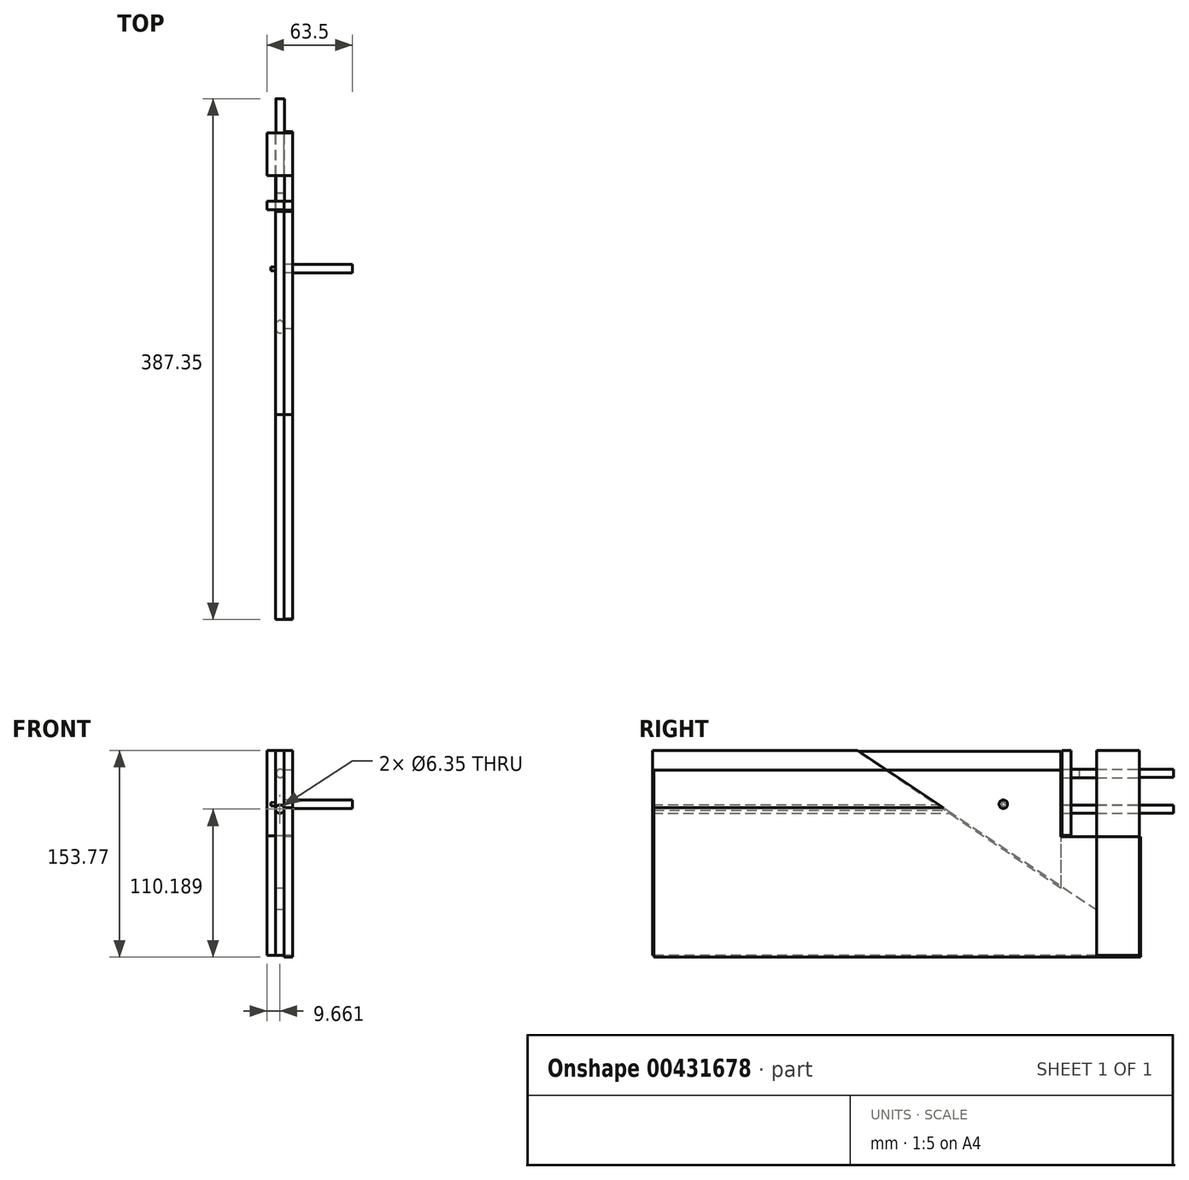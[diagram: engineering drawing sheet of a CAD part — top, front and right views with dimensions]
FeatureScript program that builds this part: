
annotation { "Feature Type Name" : "Feature", "Feature Type Description" : "" }
export const myFeature = defineFeature(function(context is Context, id is Id, definition is map)
    precondition{}
    {
        {
            var Q0;
            Q0=qCreatedBy(makeId("Right.planeOp"),FACE);
            var sketch = newSketch(context, id + "F0", { "sketchPlane" : qUnion([Q0])});
            skLineSegment(sketch, "E0.bottom", {"start": v(165.1, -76.2) * mm, "end": v(-165.1, -76.2) * mm});
            skLineSegment(sketch, "E0.left", {"start": v(165.1, -76.2) * mm, "end": v(165.1, 76.2) * mm});
            skLineSegment(sketch, "E0.right", {"start": v(-165.1, -76.2) * mm, "end": v(-165.1, 76.2) * mm});
            skPoint(sketch, "E0.middle", {"position": v(0, 0) * mm});
            skLineSegment(sketch, "E1.bottom", {"start": v(165.1, 76.2) * mm, "end": v(190.5, 76.2) * mm});
            skLineSegment(sketch, "E1.top", {"start": v(165.1, -76.2) * mm, "end": v(190.5, -76.2) * mm});
            skLineSegment(sketch, "E1.left", {"start": v(165.1, 76.2) * mm, "end": v(165.1, -76.2) * mm});
            skLineSegment(sketch, "E1.right", {"start": v(190.5, 76.2) * mm, "end": v(190.5, -76.2) * mm});
            skPoint(sketch, "E2.endSnap0", {"position": v(165.1, 0) * mm});
            skPoint(sketch, "E3.end.orphan", {"position": v(0, 76.2) * mm});
            skLineSegment(sketch, "E4", {"start": v(-165.1, 76.2) * mm, "end": v(-12.7, 76.2) * mm});
            skLineSegment(sketch, "E5", {"start": v(190.5, 76.2) * mm, "end": v(165.1, 76.2) * mm});
            skLineSegment(sketch, "E6", {"start": v(139.7, 12.7) * mm, "end": v(139.7, 76.2) * mm});
            skLineSegment(sketch, "E7", {"start": v(146.05, 76.2) * mm, "end": v(146.05, 12.7) * mm});
            skLineSegment(sketch, "E8.trimOffspring", {"start": v(146.05, 76.2) * mm, "end": v(139.7, 76.2) * mm});
            skLineSegment(sketch, "E9", {"start": v(139.7, 12.7) * mm, "end": v(146.05, 12.7) * mm});
            skPoint(sketch, "E10.orphan", {"position": v(146.05, 0) * mm});
            skPoint(sketch, "E2.end.orphan", {"position": v(139.7, 0) * mm});
            skLineSegment(sketch, "E11", {"start": v(165.1, -76.2) * mm, "end": v(165.1, -42.09) * mm});
            skLineSegment(sketch, "E12", {"start": v(-12.7, 76.2) * mm, "end": v(165.1, -42.09) * mm});
            skLineSegment(sketch, "E13", {"start": v(-12.7, 76.2) * mm, "end": v(139.7, 76.2) * mm});
            skLineSegment(sketch, "E14", {"start": v(139.7, 12.7) * mm, "end": v(139.7, -25.2) * mm});
            skSolve(sketch);
        }
        {
            var Q0;
            Q0=makeQuery(id+"F0.imprint","IMPRINT",FACE,{"disambiguationData":[TD([[makeQuery(id+"F0.imprint","IMPRINT",EDGE,{"derivedFrom":sQuery(id+"F0.wireOp",EDGE,"E6")}),-1.0]])]});
            var Q1;
            Q1=makeQuery(id+"F0.imprint","IMPRINT",FACE,{"disambiguationData":[TD([[makeQuery(id+"F0.imprint","IMPRINT",EDGE,{"derivedFrom":sQuery(id+"F0.wireOp",EDGE,"E0.bottom")}),-1.0]])]});
            var Q2;
            Q2=makeQuery(id+"F0.imprint","IMPRINT",FACE,{"disambiguationData":[TD([[makeQuery(id+"F0.imprint","IMPRINT",EDGE,{"derivedFrom":sQuery(id+"F0.wireOp",EDGE,"E1.top")}),1.0]])]});
            extrude(context, id + "F1", {"entities" : qUnion([Q0, Q1, Q2]), "depth" : 6.35 * mm});
        }
        {
            var Q0;
            Q0=makeQuery(id+"F1.opExtrude","CAP_FACE",FACE,{"disambiguationData":[OSD([sQuery(id+"F0.wireOp",EDGE,"E0.bottom"),sQuery(id+"F0.wireOp",EDGE,"E0.right"),sQuery(id+"F0.wireOp",EDGE,"E1.top"),sQuery(id+"F0.wireOp",EDGE,"E1.left"),sQuery(id+"F0.wireOp",EDGE,"E1.right"),sQuery(id+"F0.wireOp",EDGE,"E4"),sQuery(id+"F0.wireOp",EDGE,"E5"),sQuery(id+"F0.wireOp",EDGE,"E12")])],"isStart":false});
            var sketch = newSketch(context, id + "F2", { "sketchPlane" : qUnion([Q0])});
            skLineSegment(sketch, "E15.bottom", {"start": v(165.1, 76.2) * mm, "end": v(190.5, 76.2) * mm});
            skLineSegment(sketch, "E15.top", {"start": v(165.1, -76.2) * mm, "end": v(190.5, -76.2) * mm});
            skLineSegment(sketch, "E15.left", {"start": v(165.1, 76.2) * mm, "end": v(165.1, -76.2) * mm});
            skLineSegment(sketch, "E15.right", {"start": v(190.5, 76.2) * mm, "end": v(190.5, -76.2) * mm});
            skSolve(sketch);
        }
        {
            var Q0;
            Q0 = qSketchRegion(id + "F2", true);
            extrude(context, id + "F3", {"entities" : qUnion([Q0]), "operationType" : NewBodyOperationType.ADD, "depth" : 6.35 * mm});
        }
        {
            var Q0;
            Q0=makeQuery(id+"F1.opExtrude","CAP_FACE",FACE,{"disambiguationData":[OSD([sQuery(id+"F0.wireOp",EDGE,"E0.bottom"),sQuery(id+"F0.wireOp",EDGE,"E0.right"),sQuery(id+"F0.wireOp",EDGE,"E1.top"),sQuery(id+"F0.wireOp",EDGE,"E1.left"),sQuery(id+"F0.wireOp",EDGE,"E1.right"),sQuery(id+"F0.wireOp",EDGE,"E4"),sQuery(id+"F0.wireOp",EDGE,"E5"),sQuery(id+"F0.wireOp",EDGE,"E12")])],"isStart":true});
            var sketch = newSketch(context, id + "F4", { "sketchPlane" : qUnion([Q0])});
            skLineSegment(sketch, "E16.bottom", {"start": v(-190.5, 76.2) * mm, "end": v(-165.1, 76.2) * mm});
            skLineSegment(sketch, "E16.top", {"start": v(-190.5, -76.2) * mm, "end": v(-165.1, -76.2) * mm});
            skLineSegment(sketch, "E16.left", {"start": v(-190.5, 76.2) * mm, "end": v(-190.5, -76.2) * mm});
            skLineSegment(sketch, "E16.right", {"start": v(-165.1, 76.2) * mm, "end": v(-165.1, -76.2) * mm});
            skSolve(sketch);
        }
        {
            var Q0;
            Q0 = qSketchRegion(id + "F4", true);
            extrude(context, id + "F5", {"entities" : qUnion([Q0]), "operationType" : NewBodyOperationType.ADD, "depth" : 6.35 * mm});
        }
        {
            var Q0;
            Q0=makeQuery(id+"F1.opExtrude","CAP_FACE",FACE,{"disambiguationData":[OSD([sQuery(id+"F0.wireOp",EDGE,"E0.bottom"),sQuery(id+"F0.wireOp",EDGE,"E0.right"),sQuery(id+"F0.wireOp",EDGE,"E1.top"),sQuery(id+"F0.wireOp",EDGE,"E1.left"),sQuery(id+"F0.wireOp",EDGE,"E1.right"),sQuery(id+"F0.wireOp",EDGE,"E4"),sQuery(id+"F0.wireOp",EDGE,"E5"),sQuery(id+"F0.wireOp",EDGE,"E12")])],"isStart":false});
            var sketch = newSketch(context, id + "F6", { "sketchPlane" : qUnion([Q0])});
            skLineSegment(sketch, "E17.bottom", {"start": v(139.43, 76.32) * mm, "end": v(146.17, 76.32) * mm});
            skLineSegment(sketch, "E17.top", {"start": v(139.43, 13.2) * mm, "end": v(146.17, 13.2) * mm});
            skLineSegment(sketch, "E17.left", {"start": v(139.43, 76.32) * mm, "end": v(139.43, 13.2) * mm});
            skLineSegment(sketch, "E17.right", {"start": v(146.17, 76.32) * mm, "end": v(146.17, 13.2) * mm});
            skSolve(sketch);
        }
        {
            var Q0;
            Q0 = qSketchRegion(id + "F6", true);
            extrude(context, id + "F7", {"entities" : qUnion([Q0]), "operationType" : NewBodyOperationType.ADD, "depth" : 6.35 * mm});
        }
        {
            var Q0;
            Q0=makeQuery(id+"F1.opExtrude","CAP_FACE",FACE,{"disambiguationData":[OSD([sQuery(id+"F0.wireOp",EDGE,"E6"),sQuery(id+"F0.wireOp",EDGE,"E7"),sQuery(id+"F0.wireOp",EDGE,"E8.trimOffspring"),sQuery(id+"F0.wireOp",EDGE,"E9")])],"isStart":true});
            extrude(context, id + "F8", {"entities" : qUnion([Q0]), "operationType" : NewBodyOperationType.ADD, "depth" : 6.35 * mm});
        }
        {
            var Q0;
            Q0=makeQuery(id+"F5.boolean.opBoolean","MERGE",FACE,{"derivedFrom":[makeQuery(id+"F3.boolean.opBoolean","MERGE",FACE,{"derivedFrom":[makeQuery(id+"F1.opExtrude","SWEPT_FACE",FACE,{"disambiguationData":[OSD([sQuery(id+"F0.wireOp",EDGE,"E1.right")])]}),makeQuery(id+"F3.opExtrude","SWEPT_FACE",FACE,{"disambiguationData":[OSD([sQuery(id+"F2.wireOp",EDGE,"E15.right")])]})]}),makeQuery(id+"F5.opExtrude","SWEPT_FACE",FACE,{"disambiguationData":[OSD([sQuery(id+"F4.wireOp",EDGE,"E16.left")])]})]});
            var sketch = newSketch(context, id + "F9", { "sketchPlane" : qUnion([Q0])});
            skPoint(sketch, "E18", {"position": v(-3.08, 38.07) * mm});
            skSolve(sketch);
        }
        {
            var Q0;
            {var subQ0=sQuery(id+"F2.wireOp",EDGE,"E15.right");Q0=makeQuery(id+"F9.imprint","IMPRINT",FACE,{"disambiguationData":[TD([[makeQuery(id+"F9.imprint","IMPRINT",EDGE,{"derivedFrom":makeQuery(id+"F3.opExtrude","CAP_EDGE",EDGE,{"disambiguationData":[OSD([subQ0])],"isStart":false})}),1.0]])]});}
            extrude(context, id + "F10", {"entities" : qUnion([Q0]), "operationType" : NewBodyOperationType.ADD, "depth" : 6.35 * mm});
        }
        {
            var Q0;
            Q0=makeQuery(id+"F10.opExtrude","CAP_FACE",FACE,{"disambiguationData":[OSD([sQuery(id+"F0.wireOp",EDGE,"E1.top"),sQuery(id+"F0.wireOp",EDGE,"E1.right"),sQuery(id+"F0.wireOp",EDGE,"E5"),sQuery(id+"F2.wireOp",EDGE,"E15.bottom"),sQuery(id+"F2.wireOp",EDGE,"E15.top"),sQuery(id+"F2.wireOp",EDGE,"E15.right"),sQuery(id+"F4.wireOp",EDGE,"E16.bottom"),sQuery(id+"F4.wireOp",EDGE,"E16.top"),sQuery(id+"F4.wireOp",EDGE,"E16.left")])],"isStart":false});
            var sketch = newSketch(context, id + "F11", { "sketchPlane" : qUnion([Q0])});
            skCircle(sketch, "E19", {"center": v(-3.31, 32.74) * mm, "radius": 3.18 * mm});
            skSolve(sketch);
        }
        {
            var Q0;
            Q0=sQuery(id+"F11.wireOp",VERTEX,"E19.center");
            var Q1;
            Q1=makeQuery(id+"F1.opExtrude","SWEPT_BODY",BODY,{"disambiguationData":[OSD([sQuery(id+"F0.wireOp",EDGE,"E0.bottom"),sQuery(id+"F0.wireOp",EDGE,"E0.right"),sQuery(id+"F0.wireOp",EDGE,"E1.top"),sQuery(id+"F0.wireOp",EDGE,"E1.left"),sQuery(id+"F0.wireOp",EDGE,"E1.right"),sQuery(id+"F0.wireOp",EDGE,"E4"),sQuery(id+"F0.wireOp",EDGE,"E5"),sQuery(id+"F0.wireOp",EDGE,"E12")])]});
            var Q2;
            Q2=makeQuery(id+"F1.opExtrude","SWEPT_BODY",BODY,{"disambiguationData":[OSD([sQuery(id+"F0.wireOp",EDGE,"E6"),sQuery(id+"F0.wireOp",EDGE,"E7"),sQuery(id+"F0.wireOp",EDGE,"E8.trimOffspring"),sQuery(id+"F0.wireOp",EDGE,"E9")])]});
            hole(context, id + "F12", {"style" : HoleStyle.SIMPLE, "endStyle" : HoleEndStyle.THROUGH, "holeDiameter" : 6.35 * mm, "isTappedThrough" : true, "tappedDepth" : 12.7 * mm, "tapClearance" : 3, "locations" : qUnion([Q0]), "scope" : qUnion([Q1, Q2])});
        }
        {
            var Q0;
            Q0=makeQuery(id+"F10.opExtrude","CAP_FACE",FACE,{"disambiguationData":[OSD([sQuery(id+"F0.wireOp",EDGE,"E1.top"),sQuery(id+"F0.wireOp",EDGE,"E1.right"),sQuery(id+"F0.wireOp",EDGE,"E5"),sQuery(id+"F2.wireOp",EDGE,"E15.bottom"),sQuery(id+"F2.wireOp",EDGE,"E15.top"),sQuery(id+"F2.wireOp",EDGE,"E15.right"),sQuery(id+"F4.wireOp",EDGE,"E16.bottom"),sQuery(id+"F4.wireOp",EDGE,"E16.top"),sQuery(id+"F4.wireOp",EDGE,"E16.left")])],"isStart":false});
            var sketch = newSketch(context, id + "F13", { "sketchPlane" : qUnion([Q0])});
            skCircle(sketch, "E20", {"center": v(-3.31, 32.74) * mm, "radius": 3 * mm});
            skSolve(sketch);
        }
        {
            var Q0;
            Q0 = qSketchRegion(id + "F13", true);
            extrude(context, id + "F14", {"entities" : qUnion([Q0]), "oppositeDirection" : true, "depth" : 58.5 * mm});
        }
        {
            var Q0;
            Q0=makeQuery(id+"F14.opExtrude","CAP_FACE",FACE,{"disambiguationData":[OSD([sQuery(id+"F13.wireOp",EDGE,"E20")])],"isStart":true});
            extrude(context, id + "F15", {"entities" : qUnion([Q0]), "operationType" : NewBodyOperationType.ADD, "depth" : 25.4 * mm});
        }
        {
            var Q0;
            Q0=makeQuery(id+"F10.opExtrude","CAP_FACE",FACE,{"disambiguationData":[OSD([sQuery(id+"F0.wireOp",EDGE,"E1.top"),sQuery(id+"F0.wireOp",EDGE,"E1.right"),sQuery(id+"F0.wireOp",EDGE,"E5"),sQuery(id+"F2.wireOp",EDGE,"E15.bottom"),sQuery(id+"F2.wireOp",EDGE,"E15.top"),sQuery(id+"F2.wireOp",EDGE,"E15.right"),sQuery(id+"F4.wireOp",EDGE,"E16.bottom"),sQuery(id+"F4.wireOp",EDGE,"E16.top"),sQuery(id+"F4.wireOp",EDGE,"E16.left")])],"isStart":false});
            var sketch = newSketch(context, id + "F16", { "sketchPlane" : qUnion([Q0])});
            skCircle(sketch, "E21", {"center": v(-3.68, 59.03) * mm, "radius": 3.18 * mm});
            skSolve(sketch);
        }
        {
            var Q0;
            Q0=sQuery(id+"F16.wireOp",EDGE,"E21");
            extrude(context, id + "F17", {"bodyType" : ToolBodyType.SURFACE, "surfaceEntities" : qUnion([Q0]), "depth" : 25.4 * mm});
        }
        {
            var Q0;
            Q0=makeQuery(id+"F10.opExtrude","CAP_FACE",FACE,{"disambiguationData":[OSD([sQuery(id+"F0.wireOp",EDGE,"E1.top"),sQuery(id+"F0.wireOp",EDGE,"E1.right"),sQuery(id+"F0.wireOp",EDGE,"E5"),sQuery(id+"F2.wireOp",EDGE,"E15.bottom"),sQuery(id+"F2.wireOp",EDGE,"E15.top"),sQuery(id+"F2.wireOp",EDGE,"E15.right"),sQuery(id+"F4.wireOp",EDGE,"E16.bottom"),sQuery(id+"F4.wireOp",EDGE,"E16.top"),sQuery(id+"F4.wireOp",EDGE,"E16.left")])],"isStart":false});
            var sketch = newSketch(context, id + "F18", { "sketchPlane" : qUnion([Q0])});
            skCircle(sketch, "E22", {"center": v(-3.6, 59.3) * mm, "radius": 3.04 * mm});
            skSolve(sketch);
        }
        {
            var Q0;
            Q0 = qSketchRegion(id + "F18", true);
            extrude(context, id + "F19", {"entities" : qUnion([Q0]), "operationType" : NewBodyOperationType.ADD, "depth" : 25.4 * mm});
        }
        {
            var Q0;
            Q0=makeQuery(id+"F19.opExtrude","CAP_FACE",FACE,{"disambiguationData":[OSD([sQuery(id+"F18.wireOp",EDGE,"E22")])],"isStart":false});
            extrude(context, id + "F20", {"entities" : qUnion([Q0]), "operationType" : NewBodyOperationType.ADD, "oppositeDirection" : true, "depth" : 70.16 * mm});
        }
        {
            var Q0;
            Q0=makeQuery(id+"F10.opExtrude","CAP_FACE",FACE,{"disambiguationData":[OSD([sQuery(id+"F0.wireOp",EDGE,"E1.top"),sQuery(id+"F0.wireOp",EDGE,"E1.right"),sQuery(id+"F0.wireOp",EDGE,"E5"),sQuery(id+"F2.wireOp",EDGE,"E15.bottom"),sQuery(id+"F2.wireOp",EDGE,"E15.top"),sQuery(id+"F2.wireOp",EDGE,"E15.right"),sQuery(id+"F4.wireOp",EDGE,"E16.bottom"),sQuery(id+"F4.wireOp",EDGE,"E16.top"),sQuery(id+"F4.wireOp",EDGE,"E16.left")])],"isStart":false});
            var sketch = newSketch(context, id + "F21", { "sketchPlane" : qUnion([Q0])});
            skCircle(sketch, "E23", {"center": v(-3.6, 59.3) * mm, "radius": 3.15 * mm});
            skSolve(sketch);
        }
        {
            var Q0;
            Q0 = qSketchRegion(id + "F21", true);
            extrude(context, id + "F22", {"entities" : qUnion([Q0]), "oppositeDirection" : true, "depth" : 58.5 * mm});
        }
        {
            var Q0;
            Q0=qCreatedBy(makeId("Right.planeOp"),FACE);
            var sketch = newSketch(context, id + "F23", { "sketchPlane" : qUnion([Q0])});
            skLineSegment(sketch, "E24", {"start": v(-13.06, 75.72) * mm, "end": v(138.54, 75.72) * mm});
            skLineSegment(sketch, "E25", {"start": v(138.54, 75.72) * mm, "end": v(138.54, -26.34) * mm});
            skLineSegment(sketch, "E26", {"start": v(138.54, -26.34) * mm, "end": v(-13.06, 75.72) * mm});
            skSolve(sketch);
        }
        {
            var Q0;
            Q0=makeQuery(id+"F23.imprint","IMPRINT",FACE,{"disambiguationData":[TD([[makeQuery(id+"F23.imprint","IMPRINT",EDGE,{"derivedFrom":sQuery(id+"F23.wireOp",EDGE,"E24")}),-1.0]])]});
            extrude(context, id + "F24", {"entities" : qUnion([Q0]), "depth" : 6.35 * mm});
        }
        {
            var Q0;
            Q0=makeQuery(id+"F24.opExtrude","CAP_FACE",FACE,{"disambiguationData":[OSD([sQuery(id+"F23.wireOp",EDGE,"E24"),sQuery(id+"F23.wireOp",EDGE,"E25"),sQuery(id+"F23.wireOp",EDGE,"E26")])],"isStart":false});
            var sketch = newSketch(context, id + "F25", { "sketchPlane" : qUnion([Q0])});
            skCircle(sketch, "E27", {"center": v(95.75, 36.37) * mm, "radius": 3.18 * mm});
            skSolve(sketch);
        }
        {
            var Q0;
            Q0 = qSketchRegion(id + "F25", true);
            extrude(context, id + "F26", {"entities" : qUnion([Q0]), "operationType" : NewBodyOperationType.ADD, "depth" : 25.4 * mm});
        }
        {
            var Q0;
            Q0=makeQuery(id+"F26.opExtrude","CAP_FACE",FACE,{"disambiguationData":[OSD([sQuery(id+"F25.wireOp",EDGE,"E27")])],"isStart":false});
            extrude(context, id + "F27", {"entities" : qUnion([Q0]), "operationType" : NewBodyOperationType.ADD, "oppositeDirection" : true, "depth" : 35.07 * mm, "hasDraft" : true, "draftAngle" : 3 * degree, "draftPullDirection" : true, "hasSecondDirection" : true, "secondDirectionOppositeDirection" : false, "secondDirectionDepth" : 25.4 * mm});
        }
        {
            var Q0;
            {var subQ0=sQuery(id+"F0.wireOp",EDGE,"E0.right");var subQ1=sQuery(id+"F0.wireOp",EDGE,"E4");var subQ2=sQuery(id+"F0.wireOp",EDGE,"E12");Q0=makeQuery(id+"F12.hole-0.boolean.opBoolean","SPLIT",FACE,{"disambiguationData":[TD([makeQuery(id+"F1.opExtrude","SWEPT_FACE",FACE,{"disambiguationData":[OSD([subQ1])]})])],"derivedFrom":makeQuery(id+"F1.opExtrude","CAP_FACE",FACE,{"disambiguationData":[OSD([sQuery(id+"F0.wireOp",EDGE,"E0.bottom"),subQ0,sQuery(id+"F0.wireOp",EDGE,"E1.top"),sQuery(id+"F0.wireOp",EDGE,"E1.left"),sQuery(id+"F0.wireOp",EDGE,"E1.right"),subQ1,sQuery(id+"F0.wireOp",EDGE,"E5"),subQ2])],"isStart":false})});}
            var sketch = newSketch(context, id + "F28", { "sketchPlane" : qUnion([Q0])});
            skSolve(sketch);
        }
        {
            var Q0;
            Q0=makeQuery(id+"F24.opExtrude","CAP_FACE",FACE,{"disambiguationData":[OSD([sQuery(id+"F23.wireOp",EDGE,"E24"),sQuery(id+"F23.wireOp",EDGE,"E25"),sQuery(id+"F23.wireOp",EDGE,"E26")])],"isStart":false});
            var sketch = newSketch(context, id + "F29", { "sketchPlane" : qUnion([Q0])});
            skLineSegment(sketch, "E28.bottom", {"start": v(138.54, 61.78) * mm, "end": v(-164, 61.78) * mm});
            skLineSegment(sketch, "E28.top", {"start": v(138.54, -77.45) * mm, "end": v(-164, -77.45) * mm});
            skLineSegment(sketch, "E28.left", {"start": v(138.54, 61.78) * mm, "end": v(138.54, -77.45) * mm});
            skLineSegment(sketch, "E28.right", {"start": v(-164, 61.78) * mm, "end": v(-164, -77.45) * mm});
            skLineSegment(sketch, "E29", {"start": v(138.54, -77.45) * mm, "end": v(197.86, -77.45) * mm});
            skLineSegment(sketch, "E30", {"start": v(197.86, -77.45) * mm, "end": v(197.86, 0) * mm});
            skLineSegment(sketch, "E31", {"start": v(138.54, 12.07) * mm, "end": v(199.24, 12.07) * mm});
            skLineSegment(sketch, "E32", {"start": v(197.86, 12.07) * mm, "end": v(197.86, -38.73) * mm});
            skLineSegment(sketch, "E33", {"start": v(197.86, -38.73) * mm, "end": v(197.86, 12.07) * mm});
            skSolve(sketch);
        }
        {
            var Q0;
            Q0=makeQuery(id+"F29.imprint","IMPRINT",FACE,{"disambiguationData":[TD([[makeQuery(id+"F29.imprint","IMPRINT",EDGE,{"derivedFrom":makeQuery(id+"F26.opExtrude","CAP_EDGE",EDGE,{"disambiguationData":[OSD([sQuery(id+"F25.wireOp",EDGE,"E27")])],"isStart":true})}),-1.0]])]});
            var Q1;
            {var subQ0=sQuery(id+"F0.wireOp",EDGE,"E4");Q1=makeQuery(id+"F28.imprint","IMPRINT",FACE,{"disambiguationData":[TD([[makeQuery(id+"F28.imprint","IMPRINT",EDGE,{"derivedFrom":makeQuery(id+"F1.opExtrude","CAP_EDGE",EDGE,{"disambiguationData":[OSD([subQ0])],"isStart":false})}),-1.0]])]});}
            var Q2;
            Q2 = qSketchRegion(id + "F29", true);
            extrude(context, id + "F30", {"entities" : qUnion([Q0, Q1, Q2]), "depth" : 6.35 * mm});
        }
    });
